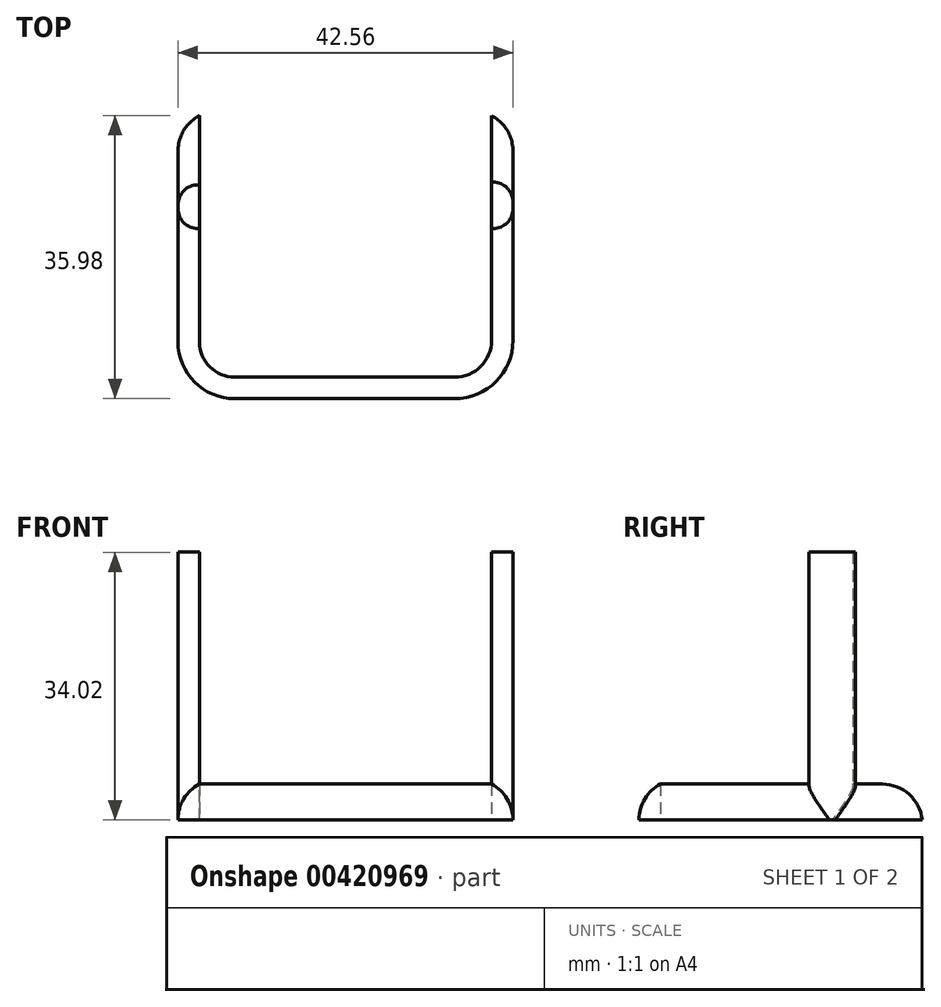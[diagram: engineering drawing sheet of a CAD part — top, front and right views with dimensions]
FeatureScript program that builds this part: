
annotation { "Feature Type Name" : "Feature", "Feature Type Description" : "" }
export const myFeature = defineFeature(function(context is Context, id is Id, definition is map)
    precondition{}
    {
        {
            var Q0;
            Q0=qCreatedBy(makeId("Top.planeOp"),FACE);
            var sketch = newSketch(context, id + "F0", { "sketchPlane" : qUnion([Q0])});
            skLineSegment(sketch, "E0", {"start": v(-37.34, 0) * mm, "end": v(-37.34, -28.76) * mm});
            skLineSegment(sketch, "E1", {"start": v(-32.73, -33.37) * mm, "end": v(-4.79, -33.37) * mm});
            skLineSegment(sketch, "E2", {"start": v(0, -28.58) * mm, "end": v(0, 0) * mm});
            skPoint(sketch, "E3.visualSharp", {"position": v(-37.34, -33.37) * mm});
            skArc(sketch, "E3.filletArc", {"start": v(-37.34, -28.76) * mm, "mid": v(-36, -32.02) * mm, "end": v(-32.73, -33.37) * mm});
            skPoint(sketch, "E4.visualSharp", {"position": v(0, -33.37) * mm});
            skArc(sketch, "E4.filletArc", {"start": v(-4.79, -33.37) * mm, "mid": v(-1.4, -31.97) * mm, "end": v(0, -28.58) * mm});
            skSolve(sketch);
        }
        {
            var Q0;
            Q0=qCreatedBy(makeId("Front.planeOp"),FACE);
            var sketch = newSketch(context, id + "F1", { "sketchPlane" : qUnion([Q0])});
            skLineSegment(sketch, "E5.bottom", {"start": v(-37.22, 0) * mm, "end": v(-39.95, 0) * mm});
            skLineSegment(sketch, "E5.top", {"start": v(-37.22, -4.56) * mm, "end": v(-39.95, -4.56) * mm});
            skLineSegment(sketch, "E5.left", {"start": v(-37.22, 0) * mm, "end": v(-37.22, -4.56) * mm});
            skLineSegment(sketch, "E5.right", {"start": v(-39.95, 0) * mm, "end": v(-39.95, -4.56) * mm});
            skSolve(sketch);
        }
        {
            var Q0;
            Q0=makeQuery(id+"F1.imprint","IMPRINT",FACE,{"disambiguationData":[TD([[makeQuery(id+"F1.imprint","IMPRINT",EDGE,{"derivedFrom":sQuery(id+"F1.wireOp",EDGE,"E5.bottom")}),1.0]])]});
            var Q1;
            Q1=sQuery(id+"F0.wireOp",EDGE,"E0");
            var Q2;
            Q2=sQuery(id+"F0.wireOp",EDGE,"E3.filletArc");
            var Q3;
            Q3=sQuery(id+"F0.wireOp",EDGE,"E1");
            var Q4;
            Q4=sQuery(id+"F0.wireOp",EDGE,"E4.filletArc");
            var Q5;
            Q5=sQuery(id+"F0.wireOp",EDGE,"E2");
            sweep(context, id + "F2", {"profiles" : qUnion([Q0]), "path" : qUnion([Q1, Q2, Q3, Q4, Q5])});
        }
        {
            var Q0;
            Q0=makeQuery(id+"F2.opSweep","SWEPT_FACE",FACE,{"disambiguationData":[OSD([sQuery(id+"F0.wireOp",EDGE,"E0"),sQuery(id+"F1.wireOp",EDGE,"E5.bottom")])]});
            var sketch = newSketch(context, id + "F3", { "sketchPlane" : qUnion([Q0])});
            skLineSegment(sketch, "E6.bottom", {"start": v(-39.95, -8.82) * mm, "end": v(-37.22, -8.82) * mm});
            skLineSegment(sketch, "E6.top", {"start": v(-39.95, -14.38) * mm, "end": v(-37.22, -14.38) * mm});
            skLineSegment(sketch, "E6.left", {"start": v(-39.95, -8.82) * mm, "end": v(-39.95, -14.38) * mm});
            skLineSegment(sketch, "E6.right", {"start": v(-37.22, -8.82) * mm, "end": v(-37.22, -14.38) * mm});
            skPoint(sketch, "E7.firstSnap0", {"position": v(-0.13, -14.3) * mm});
            skLineSegment(sketch, "E7.bottom", {"start": v(-0.13, -14.38) * mm, "end": v(2.61, -14.38) * mm});
            skLineSegment(sketch, "E7.top", {"start": v(-0.13, -8.47) * mm, "end": v(2.61, -8.47) * mm});
            skLineSegment(sketch, "E7.left", {"start": v(-0.13, -14.38) * mm, "end": v(-0.13, -8.47) * mm});
            skLineSegment(sketch, "E7.right", {"start": v(2.61, -14.38) * mm, "end": v(2.61, -8.47) * mm});
            skSolve(sketch);
        }
        {
            var Q0;
            Q0 = qSketchRegion(id + "F3", true);
            extrude(context, id + "F4", {"entities" : qUnion([Q0]), "operationType" : NewBodyOperationType.ADD, "depth" : 29.46 * mm});
        }
        {
            var Q0;
            Q0=makeQuery(id+"F4.opExtrude","SWEPT_EDGE",EDGE,{"disambiguationData":[OSD([sQuery(id+"F0.wireOp",EDGE,"E0"),sQuery(id+"F1.wireOp",EDGE,"E5.bottom"),sQuery(id+"F1.wireOp",EDGE,"E5.right"),sQuery(id+"F3.wireOp",EDGE,"E6.top"),sQuery(id+"F3.wireOp",EDGE,"E6.left")])]});
            fillet(context, id + "F5", {"entities" : qUnion([Q0]), "radius" : 2.54 * mm, "tangentPropagation" : true, "allowEdgeOverflow" : false});
        }
        {
            var Q0;
            Q0=makeQuery(id+"F4.opExtrude","SWEPT_EDGE",EDGE,{"disambiguationData":[OSD([sQuery(id+"F0.wireOp",EDGE,"E2"),sQuery(id+"F1.wireOp",EDGE,"E5.bottom"),sQuery(id+"F1.wireOp",EDGE,"E5.right"),sQuery(id+"F3.wireOp",EDGE,"E7.bottom"),sQuery(id+"F3.wireOp",EDGE,"E7.right")])]});
            fillet(context, id + "F6", {"entities" : qUnion([Q0]), "radius" : 2.54 * mm, "tangentPropagation" : true, "allowEdgeOverflow" : false});
        }
        {
            var Q0;
            Q0=makeQuery(id+"F4.opExtrude","SWEPT_EDGE",EDGE,{"disambiguationData":[OSD([sQuery(id+"F0.wireOp",EDGE,"E2"),sQuery(id+"F1.wireOp",EDGE,"E5.bottom"),sQuery(id+"F1.wireOp",EDGE,"E5.right"),sQuery(id+"F3.wireOp",EDGE,"E7.top"),sQuery(id+"F3.wireOp",EDGE,"E7.right")])]});
            fillet(context, id + "F7", {"entities" : qUnion([Q0]), "radius" : 2.54 * mm, "tangentPropagation" : true, "allowEdgeOverflow" : false});
        }
        {
            var Q0;
            Q0=makeQuery(id+"F4.opExtrude","SWEPT_EDGE",EDGE,{"disambiguationData":[OSD([sQuery(id+"F0.wireOp",EDGE,"E0"),sQuery(id+"F1.wireOp",EDGE,"E5.bottom"),sQuery(id+"F1.wireOp",EDGE,"E5.right"),sQuery(id+"F3.wireOp",EDGE,"E6.bottom"),sQuery(id+"F3.wireOp",EDGE,"E6.left")])]});
            fillet(context, id + "F8", {"entities" : qUnion([Q0]), "radius" : 2.54 * mm, "tangentPropagation" : true, "allowEdgeOverflow" : false});
        }
        {
            var Q0;
            Q0=makeQuery(id+"F2.opSweep","CAP_EDGE",EDGE,{"disambiguationData":[OSD([sQuery(id+"F0.wireOp",VERTEX,"E0.start"),sQuery(id+"F1.wireOp",EDGE,"E5.bottom")])],"isStart":true});
            fillet(context, id + "F9", {"entities" : qUnion([Q0]), "radius" : 5.08 * mm, "tangentPropagation" : true, "allowEdgeOverflow" : false});
        }
        {
            var Q0;
            Q0=makeQuery(id+"F2.opSweep","CAP_EDGE",EDGE,{"disambiguationData":[OSD([sQuery(id+"F0.wireOp",VERTEX,"E2.end"),sQuery(id+"F1.wireOp",EDGE,"E5.bottom")])],"isStart":false});
            fillet(context, id + "F10", {"entities" : qUnion([Q0]), "radius" : 5.08 * mm, "tangentPropagation" : true, "allowEdgeOverflow" : false});
        }
        {
            var Q0;
            {var subQ0=sQuery(id+"F1.wireOp",EDGE,"E5.right");var subQ1=sQuery(id+"F0.wireOp",EDGE,"E2");var subQ2=sQuery(id+"F1.wireOp",EDGE,"E5.bottom");Q0=makeQuery(id+"F4.boolean.opBoolean","SPLIT",EDGE,{"disambiguationData":[TD([makeQuery(id+"F4.opExtrude","SWEPT_FACE",FACE,{"disambiguationData":[OSD([sQuery(id+"F3.wireOp",EDGE,"E7.top")])]})])],"derivedFrom":makeQuery(id+"F2.opSweep","SWEPT_EDGE",EDGE,{"disambiguationData":[OSD([subQ1,subQ2,subQ0])]})});}
            fillet(context, id + "F11", {"entities" : qUnion([Q0]), "radius" : 5.08 * mm, "tangentPropagation" : true, "allowEdgeOverflow" : false});
        }
        {
            var Q0;
            {var subQ0=sQuery(id+"F1.wireOp",EDGE,"E5.right");var subQ1=sQuery(id+"F1.wireOp",EDGE,"E5.bottom");var subQ2=sQuery(id+"F0.wireOp",EDGE,"E2");Q0=makeQuery(id+"F4.boolean.opBoolean","SPLIT",EDGE,{"disambiguationData":[TD([makeQuery(id+"F4.opExtrude","SWEPT_FACE",FACE,{"disambiguationData":[OSD([sQuery(id+"F3.wireOp",EDGE,"E7.bottom")])]})])],"derivedFrom":makeQuery(id+"F2.opSweep","SWEPT_EDGE",EDGE,{"disambiguationData":[OSD([subQ2,subQ1,subQ0])]})});}
            fillet(context, id + "F12", {"entities" : qUnion([Q0]), "radius" : 5.08 * mm, "tangentPropagation" : true, "allowEdgeOverflow" : false});
        }
        {
            var Q0;
            {var subQ0=sQuery(id+"F1.wireOp",EDGE,"E5.bottom");var subQ1=sQuery(id+"F0.wireOp",EDGE,"E0");var subQ2=sQuery(id+"F1.wireOp",EDGE,"E5.right");Q0=makeQuery(id+"F4.boolean.opBoolean","SPLIT",EDGE,{"disambiguationData":[TD([makeQuery(id+"F4.opExtrude","SWEPT_FACE",FACE,{"disambiguationData":[OSD([sQuery(id+"F3.wireOp",EDGE,"E6.bottom")])]})])],"derivedFrom":makeQuery(id+"F2.opSweep","SWEPT_EDGE",EDGE,{"disambiguationData":[OSD([subQ1,subQ0,subQ2])]})});}
            fillet(context, id + "F13", {"entities" : qUnion([Q0]), "radius" : 5.08 * mm, "tangentPropagation" : true, "allowEdgeOverflow" : false});
        }
    });
